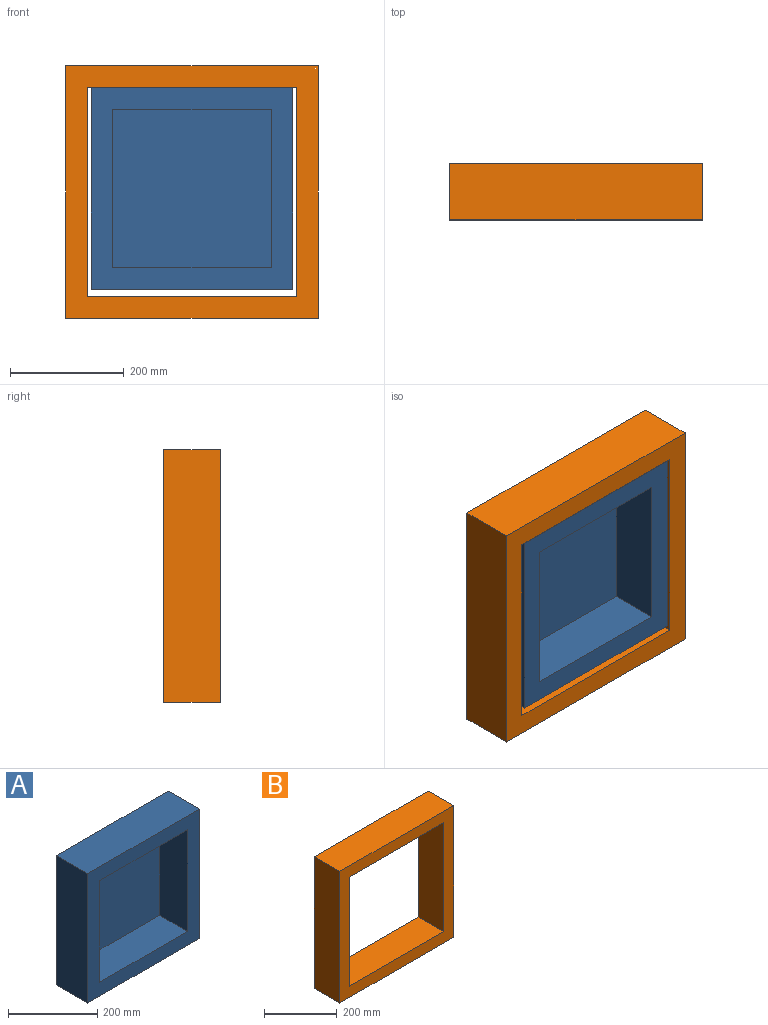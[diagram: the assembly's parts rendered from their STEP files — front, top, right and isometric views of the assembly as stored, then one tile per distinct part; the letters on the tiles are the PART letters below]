
ASSEMBLY  parts=2 mates=1
PART A: 11 faces, bbox 355.6x99.1x355.6 mm
  f0: plane 355.6x99.06mm, normal (0,0,-1), area 35225.7mm2, adj f1,f7,f8,f10
  f1: plane 355.6x99.06mm, normal (1,0,0), area 35225.7mm2, adj f0,f2,f8,f10
  f2: plane 355.6x99.06mm, normal (0,0,1), area 35225.7mm2, adj f1,f7,f8,f10
  f3: plane 279.4x88.9mm, normal (-1,0,0), area 24838.7mm2, adj f4,f6,f8,f9
  f4: plane 279.4x88.9mm, normal (0,0,1), area 24838.7mm2, adj f3,f5,f8,f9
  f5: plane 279.4x88.9mm, normal (1,0,0), area 24838.7mm2, adj f4,f6,f8,f9
  f6: plane 279.4x88.9mm, normal (0,0,-1), area 24838.7mm2, adj f3,f5,f8,f9
  f7: plane 355.6x99.06mm, normal (-1,0,0), area 35225.7mm2, adj f0,f2,f8,f10
  f8: plane 355.6x355.6mm, normal (0,-1,0), area 48387mm2, adj f0,f1,f2,f3,f4,f5,f6,f7
  f9: plane 279.4x279.4mm, normal (0,-1,0), area 78064.4mm2, adj f3,f4,f5,f6
  f10: plane 355.6x355.6mm, normal (0,1,0), area 126451.4mm2, adj f0,f1,f2,f7
PART B: 10 faces, bbox 444.5x99.1x444.5 mm
  f0: plane 368.3x99.06mm, normal (0,0,1), area 36483.8mm2, adj f1,f7,f8,f9
  f1: plane 368.3x99.06mm, normal (1,0,0), area 36483.8mm2, adj f0,f2,f8,f9
  f2: plane 368.3x99.06mm, normal (0,0,-1), area 36483.8mm2, adj f1,f7,f8,f9
  f3: plane 444.5x99.06mm, normal (0,0,-1), area 44032.2mm2, adj f4,f6,f8,f9
  f4: plane 444.5x99.06mm, normal (1,0,0), area 44032.2mm2, adj f3,f5,f8,f9
  f5: plane 444.5x99.06mm, normal (0,0,1), area 44032.2mm2, adj f4,f6,f8,f9
  f6: plane 444.5x99.06mm, normal (-1,0,0), area 44032.2mm2, adj f3,f5,f8,f9
  f7: plane 368.3x99.06mm, normal (-1,0,0), area 36483.8mm2, adj f0,f2,f8,f9
  f8: plane 444.5x444.5mm, normal (0,-1,0), area 61935.4mm2, adj f0,f1,f2,f3,f4,f5,f6,f7
  f9: plane 444.5x444.5mm, normal (0,1,0), area 61935.4mm2, adj f0,f1,f2,f3,f4,f5,f6,f7
PLACE A t=(0,99.06,6.35)mm
PLACE B t=(0,99.06,0)mm
MATE ball B.f8 <-> A.f8  axis (0,-1,0) through (184.15,0,368.3)mm
